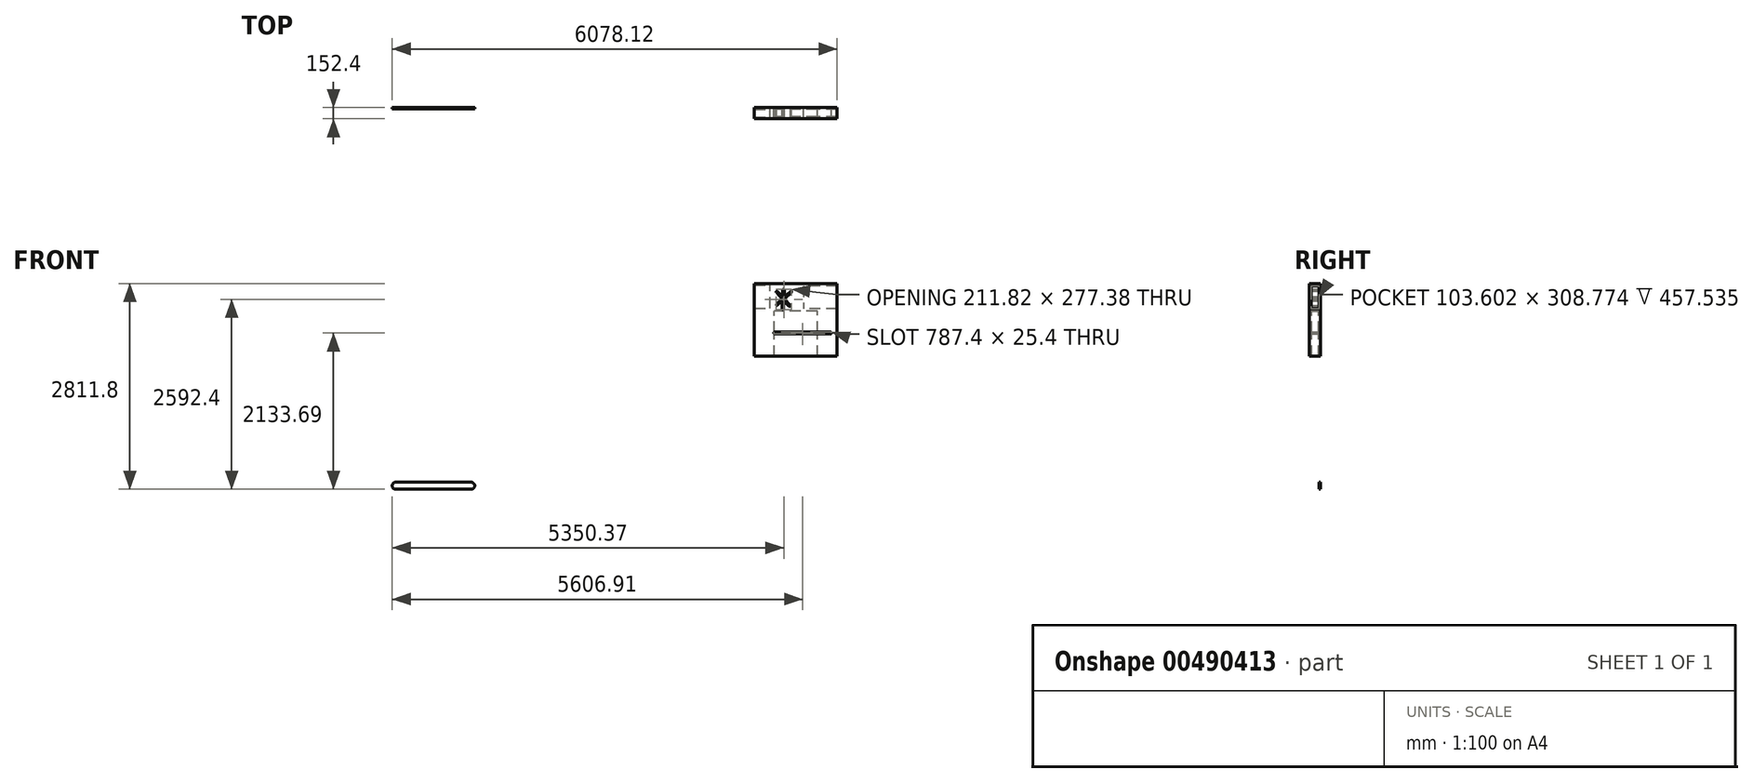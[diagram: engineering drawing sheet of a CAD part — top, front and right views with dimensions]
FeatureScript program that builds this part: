
annotation { "Feature Type Name" : "Feature", "Feature Type Description" : "" }
export const myFeature = defineFeature(function(context is Context, id is Id, definition is map)
    precondition{}
    {
        {
            var Q0;
            Q0=qCreatedBy(makeId("Front.planeOp"),FACE);
            var sketch = newSketch(context, id + "F0", { "sketchPlane" : qUnion([Q0])});
            skLineSegment(sketch, "E0", {"start": v(-90.37, 91.22) * mm, "end": v(82.7, -95.7) * mm});
            skLineSegment(sketch, "E1", {"start": v(100.5, 92) * mm, "end": v(-86.4, -81.06) * mm});
            skLineSegment(sketch, "E2", {"start": v(-83.93, -8.2) * mm, "end": v(89.84, -8.2) * mm});
            skLineSegment(sketch, "E3", {"start": v(0, 116.2) * mm, "end": v(-9.79, -138.34) * mm});
            skArc(sketch, "E4.0.startCap", {"start": v(-11.42, 116.64) * mm, "mid": v(0.44, 127.62) * mm, "end": v(11.42, 115.76) * mm});
            skArc(sketch, "E4.0.endCap", {"start": v(1.63, -138.78) * mm, "mid": v(-10.23, -149.76) * mm, "end": v(-21.21, -137.9) * mm});
            skLineSegment(sketch, "E4.0.left", {"start": v(11.42, 115.76) * mm, "end": v(1.63, -138.78) * mm});
            skLineSegment(sketch, "E4.0.right", {"start": v(-11.42, 116.64) * mm, "end": v(-21.21, -137.9) * mm});
            skArc(sketch, "E5.0.startCap", {"start": v(93.17, 99.93) * mm, "mid": v(108.42, 99.34) * mm, "end": v(107.84, 84.09) * mm});
            skArc(sketch, "E5.0.endCap", {"start": v(-79.07, -88.98) * mm, "mid": v(-94.33, -88.4) * mm, "end": v(-93.74, -73.14) * mm});
            skLineSegment(sketch, "E5.0.left", {"start": v(107.84, 84.09) * mm, "end": v(-79.07, -88.98) * mm});
            skLineSegment(sketch, "E5.0.right", {"start": v(93.17, 99.93) * mm, "end": v(-93.74, -73.14) * mm});
            skArc(sketch, "E6.0.startCap", {"start": v(-97.83, 84.31) * mm, "mid": v(-97.28, 98.67) * mm, "end": v(-82.92, 98.12) * mm});
            skArc(sketch, "E6.0.endCap", {"start": v(90.15, -88.79) * mm, "mid": v(89.6, -103.15) * mm, "end": v(75.24, -102.6) * mm});
            skLineSegment(sketch, "E6.0.left", {"start": v(-82.92, 98.12) * mm, "end": v(90.15, -88.79) * mm});
            skLineSegment(sketch, "E6.0.right", {"start": v(-97.83, 84.31) * mm, "end": v(75.24, -102.6) * mm});
            skLineSegment(sketch, "E7.bottom", {"start": v(-183.07, -168.36) * mm, "end": v(275.6, -168.36) * mm});
            skLineSegment(sketch, "E7.top", {"start": v(-183.07, 208.33) * mm, "end": v(275.6, 208.33) * mm});
            skLineSegment(sketch, "E7.left", {"start": v(-183.07, -168.36) * mm, "end": v(-183.07, 208.33) * mm});
            skLineSegment(sketch, "E7.right", {"start": v(275.6, -168.36) * mm, "end": v(275.6, 208.33) * mm});
            skSolve(sketch);
        }
        {
            var Q0;
            Q0 = qSketchRegion(id + "F0", true);
            extrude(context, id + "F1", {"entities" : qUnion([Q0]), "depth" : 152.4 * mm});
        }
        {
            var Q0;
            Q0=makeQuery(id+"F1.opExtrude","SWEPT_FACE",FACE,{"disambiguationData":[OSD([sQuery(id+"F0.wireOp",EDGE,"E7.left")])]});
            var sketch = newSketch(context, id + "F2", { "sketchPlane" : qUnion([Q0])});
            skLineSegment(sketch, "E8.0", {"start": v(152.4, -168.36) * mm, "end": v(152.4, 208.33) * mm});
            skLineSegment(sketch, "E9.0", {"start": v(152.4, 208.33) * mm, "end": v(0, 208.33) * mm});
            skPoint(sketch, "E10.0", {"position": v(152.4, -168.36) * mm});
            skLineSegment(sketch, "E11.0.1", {"start": v(0, -168.36) * mm, "end": v(152.4, -168.36) * mm});
            skLineSegment(sketch, "E11.0.3", {"start": v(152.4, -168.36) * mm, "end": v(0, -168.36) * mm});
            skLineSegment(sketch, "E12.0", {"start": v(0, -168.36) * mm, "end": v(0, 208.33) * mm});
            skPoint(sketch, "E13", {"position": v(76.2, 30.31) * mm});
            skPoint(sketch, "E13.positionSnap0", {"position": v(76.2, 208.33) * mm});
            skLineSegment(sketch, "E14.bottom", {"start": v(129.3, -128.74) * mm, "end": v(23.1, -128.74) * mm});
            skLineSegment(sketch, "E14.top", {"start": v(129.3, 189.36) * mm, "end": v(23.1, 189.36) * mm});
            skLineSegment(sketch, "E14.left", {"start": v(129.3, -128.74) * mm, "end": v(129.3, 189.36) * mm});
            skLineSegment(sketch, "E14.right", {"start": v(23.1, -128.74) * mm, "end": v(23.1, 189.36) * mm});
            skSolve(sketch);
        }
        {
            var Q0;
            Q0 = qSketchRegion(id + "F2", true);
            extrude(context, id + "F3", {"entities" : qUnion([Q0]), "operationType" : NewBodyOperationType.ADD, "depth" : 213.98 * mm});
        }
        {
            var Q0;
            Q0=makeQuery(id+"F1.opExtrude","SWEPT_FACE",FACE,{"disambiguationData":[OSD([sQuery(id+"F0.wireOp",EDGE,"E7.right")])]});
            var sketch = newSketch(context, id + "F4", { "sketchPlane" : qUnion([Q0])});
            skLineSegment(sketch, "E15.0", {"start": v(-152.4, -168.36) * mm, "end": v(-152.4, 208.33) * mm});
            skLineSegment(sketch, "E16.0", {"start": v(-152.4, -168.36) * mm, "end": v(0, -168.36) * mm});
            skLineSegment(sketch, "E17.0", {"start": v(0, -168.36) * mm, "end": v(0, 208.33) * mm});
            skPoint(sketch, "E18", {"position": v(-76.2, 19.98) * mm});
            skPoint(sketch, "E18.positionSnap0", {"position": v(-76.2, 208.33) * mm});
            skPoint(sketch, "E18.positionSnap1", {"position": v(-152.4, 19.98) * mm});
            skLineSegment(sketch, "E19.bottom", {"start": v(-128, 174.37) * mm, "end": v(-24.4, 174.37) * mm});
            skLineSegment(sketch, "E19.top", {"start": v(-128, -134.4) * mm, "end": v(-24.4, -134.4) * mm});
            skLineSegment(sketch, "E19.left", {"start": v(-128, 174.37) * mm, "end": v(-128, -134.4) * mm});
            skLineSegment(sketch, "E19.right", {"start": v(-24.4, 174.37) * mm, "end": v(-24.4, -134.4) * mm});
            skSolve(sketch);
        }
        {
            var Q0;
            Q0=makeQuery(id+"F4.imprint","IMPRINT",FACE,{"disambiguationData":[TD([[makeQuery(id+"F4.imprint","IMPRINT",EDGE,{"derivedFrom":sQuery(id+"F4.wireOp",EDGE,"E15.0")}),-1.0]])]});
            extrude(context, id + "F5", {"entities" : qUnion([Q0]), "operationType" : NewBodyOperationType.ADD, "depth" : 457.54 * mm});
        }
        {
            var Q0;
            Q0=makeQuery(id+"F5.boolean.opBoolean","MERGE",FACE,{"derivedFrom":[makeQuery(id+"F3.boolean.opBoolean","MERGE",FACE,{"derivedFrom":[makeQuery(id+"F1.opExtrude","SWEPT_FACE",FACE,{"disambiguationData":[OSD([sQuery(id+"F0.wireOp",EDGE,"E7.bottom")])]}),makeQuery(id+"F3.opExtrude","SWEPT_FACE",FACE,{"disambiguationData":[OSD([sQuery(id+"F2.wireOp",EDGE,"E11.0.3")])]})]}),makeQuery(id+"F5.opExtrude","SWEPT_FACE",FACE,{"disambiguationData":[OSD([sQuery(id+"F4.wireOp",EDGE,"E16.0")])]})]});
            var sketch = newSketch(context, id + "F6", { "sketchPlane" : qUnion([Q0])});
            skLineSegment(sketch, "E20.0", {"start": v(-397.05, 152.4) * mm, "end": v(-397.05, 0) * mm});
            skPoint(sketch, "E21.0", {"position": v(-97.83, 0) * mm});
            skPoint(sketch, "E22.0", {"position": v(-79.07, 152.4) * mm});
            skLineSegment(sketch, "E23.0", {"start": v(733.13, 152.4) * mm, "end": v(733.13, 0) * mm});
            skLineSegment(sketch, "E24.0.0", {"start": v(733.13, 152.4) * mm, "end": v(-397.05, 152.4) * mm});
            skLineSegment(sketch, "E24.0.2", {"start": v(-397.05, 152.4) * mm, "end": v(733.13, 152.4) * mm});
            skLineSegment(sketch, "E25.0", {"start": v(-397.05, 0) * mm, "end": v(733.13, 0) * mm});
            skPoint(sketch, "E26", {"position": v(168.04, 76.2) * mm});
            skPoint(sketch, "E26.positionSnap0", {"position": v(733.13, 76.2) * mm});
            skPoint(sketch, "E26.positionSnap1", {"position": v(168.04, 152.4) * mm});
            skLineSegment(sketch, "E27.bottom", {"start": v(463.81, 126.04) * mm, "end": v(-127.73, 126.04) * mm});
            skLineSegment(sketch, "E27.top", {"start": v(463.81, 26.36) * mm, "end": v(-127.73, 26.36) * mm});
            skLineSegment(sketch, "E27.left", {"start": v(463.81, 126.04) * mm, "end": v(463.81, 26.36) * mm});
            skLineSegment(sketch, "E27.right", {"start": v(-127.73, 126.04) * mm, "end": v(-127.73, 26.36) * mm});
            skSolve(sketch);
        }
        {
            var Q0;
            Q0 = qSketchRegion(id + "F6", true);
            extrude(context, id + "F7", {"entities" : qUnion([Q0]), "operationType" : NewBodyOperationType.ADD, "depth" : 618.93 * mm});
        }
        {
            var Q0;
            Q0=makeQuery(id+"F7.boolean.opBoolean","MERGE",FACE,{"derivedFrom":[makeQuery(id+"F5.boolean.opBoolean","MERGE",FACE,{"derivedFrom":[makeQuery(id+"F3.boolean.opBoolean","MERGE",FACE,{"derivedFrom":[makeQuery(id+"F1.opExtrude","CAP_FACE",FACE,{"disambiguationData":[OSD([sQuery(id+"F0.wireOp",EDGE,"E4.0.startCap"),sQuery(id+"F0.wireOp",EDGE,"E4.0.endCap"),sQuery(id+"F0.wireOp",EDGE,"E4.0.left"),sQuery(id+"F0.wireOp",EDGE,"E4.0.right"),sQuery(id+"F0.wireOp",EDGE,"E5.0.startCap"),sQuery(id+"F0.wireOp",EDGE,"E5.0.endCap"),sQuery(id+"F0.wireOp",EDGE,"E5.0.left"),sQuery(id+"F0.wireOp",EDGE,"E5.0.right"),sQuery(id+"F0.wireOp",EDGE,"E6.0.startCap"),sQuery(id+"F0.wireOp",EDGE,"E6.0.endCap"),sQuery(id+"F0.wireOp",EDGE,"E6.0.left"),sQuery(id+"F0.wireOp",EDGE,"E6.0.right"),sQuery(id+"F0.wireOp",EDGE,"E7.bottom"),sQuery(id+"F0.wireOp",EDGE,"E7.top"),sQuery(id+"F0.wireOp",EDGE,"E7.left"),sQuery(id+"F0.wireOp",EDGE,"E7.right")])],"isStart":true}),makeQuery(id+"F3.opExtrude","SWEPT_FACE",FACE,{"disambiguationData":[OSD([sQuery(id+"F2.wireOp",EDGE,"E12.0")])]})]}),makeQuery(id+"F5.opExtrude","SWEPT_FACE",FACE,{"disambiguationData":[OSD([sQuery(id+"F4.wireOp",EDGE,"E17.0")])]})]}),makeQuery(id+"F7.opExtrude","SWEPT_FACE",FACE,{"disambiguationData":[OSD([sQuery(id+"F6.wireOp",EDGE,"E25.0")])]})]});
            var sketch = newSketch(context, id + "F8", { "sketchPlane" : qUnion([Q0])});
            skLineSegment(sketch, "E28", {"start": v(-642.92, -469.78) * mm, "end": v(119.08, -469.78) * mm});
            skArc(sketch, "E29.0.startCap", {"start": v(-642.92, -482.48) * mm, "mid": v(-655.62, -469.78) * mm, "end": v(-642.92, -457.08) * mm});
            skArc(sketch, "E29.0.endCap", {"start": v(119.08, -457.08) * mm, "mid": v(131.78, -469.78) * mm, "end": v(119.08, -482.48) * mm});
            skLineSegment(sketch, "E29.0.left", {"start": v(-642.92, -457.08) * mm, "end": v(119.08, -457.08) * mm});
            skLineSegment(sketch, "E29.0.right", {"start": v(-642.92, -482.48) * mm, "end": v(119.08, -482.48) * mm});
            skSolve(sketch);
        }
        {
            var Q0;
            Q0 = qSketchRegion(id + "F8", true);
            extrude(context, id + "F9", {"entities" : qUnion([Q0]), "operationType" : NewBodyOperationType.REMOVE, "endBound" : BoundingType.THROUGH_ALL, "oppositeDirection" : true, "depth" : 25.4 * mm});
        }
        {
            var Q0;
            Q0=qCreatedBy(makeId("Front.planeOp"),FACE);
            var sketch = newSketch(context, id + "F10", { "sketchPlane" : qUnion([Q0])});
            skLineSegment(sketch, "E30.bottom", {"start": v(-1517.68, -381.27) * mm, "end": v(-2787.68, -381.27) * mm});
            skLineSegment(sketch, "E30.top", {"start": v(-1517.68, 126.73) * mm, "end": v(-2787.68, 126.73) * mm});
            skLineSegment(sketch, "E30.left", {"start": v(-1263.68, -127.27) * mm, "end": v(-1263.68, -127.27) * mm});
            skLineSegment(sketch, "E30.right", {"start": v(-3041.68, -127.27) * mm, "end": v(-3041.68, -127.27) * mm});
            skPoint(sketch, "E31.visualSharp", {"position": v(-1263.68, 126.73) * mm});
            skArc(sketch, "E31.filletArc", {"start": v(-1263.68, -127.27) * mm, "mid": v(-1338.07, 52.34) * mm, "end": v(-1517.68, 126.73) * mm});
            skPoint(sketch, "E32.visualSharp", {"position": v(-1263.68, -381.27) * mm});
            skArc(sketch, "E32.filletArc", {"start": v(-1517.68, -381.27) * mm, "mid": v(-1338.07, -306.87) * mm, "end": v(-1263.68, -127.27) * mm});
            skPoint(sketch, "E33.visualSharp", {"position": v(-3041.68, 126.73) * mm});
            skArc(sketch, "E33.filletArc", {"start": v(-2787.68, 126.73) * mm, "mid": v(-2967.28, 52.34) * mm, "end": v(-3041.68, -127.27) * mm});
            skPoint(sketch, "E34.visualSharp", {"position": v(-3041.68, -381.27) * mm});
            skArc(sketch, "E34.filletArc", {"start": v(-3041.68, -127.27) * mm, "mid": v(-2967.28, -306.87) * mm, "end": v(-2787.68, -381.27) * mm});
            skLineSegment(sketch, "E35.bottom", {"start": v(-4265.49, -2603.47) * mm, "end": v(-5297.36, -2603.47) * mm});
            skLineSegment(sketch, "E35.top", {"start": v(-4265.49, -2508.22) * mm, "end": v(-5297.36, -2508.22) * mm});
            skLineSegment(sketch, "E35.left", {"start": v(-4217.86, -2555.84) * mm, "end": v(-4217.86, -2555.84) * mm});
            skLineSegment(sketch, "E35.right", {"start": v(-5344.99, -2555.84) * mm, "end": v(-5344.99, -2555.84) * mm});
            skPoint(sketch, "E36.visualSharp", {"position": v(-4217.86, -2508.22) * mm});
            skArc(sketch, "E36.filletArc", {"start": v(-4217.86, -2555.84) * mm, "mid": v(-4231.81, -2522.16) * mm, "end": v(-4265.49, -2508.22) * mm});
            skPoint(sketch, "E37.visualSharp", {"position": v(-4217.86, -2603.47) * mm});
            skArc(sketch, "E37.filletArc", {"start": v(-4265.49, -2603.47) * mm, "mid": v(-4231.81, -2589.52) * mm, "end": v(-4217.86, -2555.84) * mm});
            skPoint(sketch, "E38.visualSharp", {"position": v(-5344.99, -2508.22) * mm});
            skArc(sketch, "E38.filletArc", {"start": v(-5297.36, -2508.22) * mm, "mid": v(-5331.04, -2522.16) * mm, "end": v(-5344.99, -2555.84) * mm});
            skPoint(sketch, "E39.visualSharp", {"position": v(-5344.99, -2603.47) * mm});
            skArc(sketch, "E39.filletArc", {"start": v(-5344.99, -2555.84) * mm, "mid": v(-5331.04, -2589.52) * mm, "end": v(-5297.36, -2603.47) * mm});
            skLineSegment(sketch, "E40", {"start": v(-4198.68, -2755.35) * mm, "end": v(-5325.8, -2755.35) * mm});
            skSolve(sketch);
        }
        {
            var Q0;
            Q0=makeQuery(id+"F10.imprint","IMPRINT",FACE,{"disambiguationData":[TD([[makeQuery(id+"F10.imprint","IMPRINT",EDGE,{"derivedFrom":sQuery(id+"F10.wireOp",EDGE,"E35.bottom")}),-1.0]])]});
            extrude(context, id + "F11", {"entities" : qUnion([Q0]), "depth" : (0.08) * 254 * mm});
        }
    });
